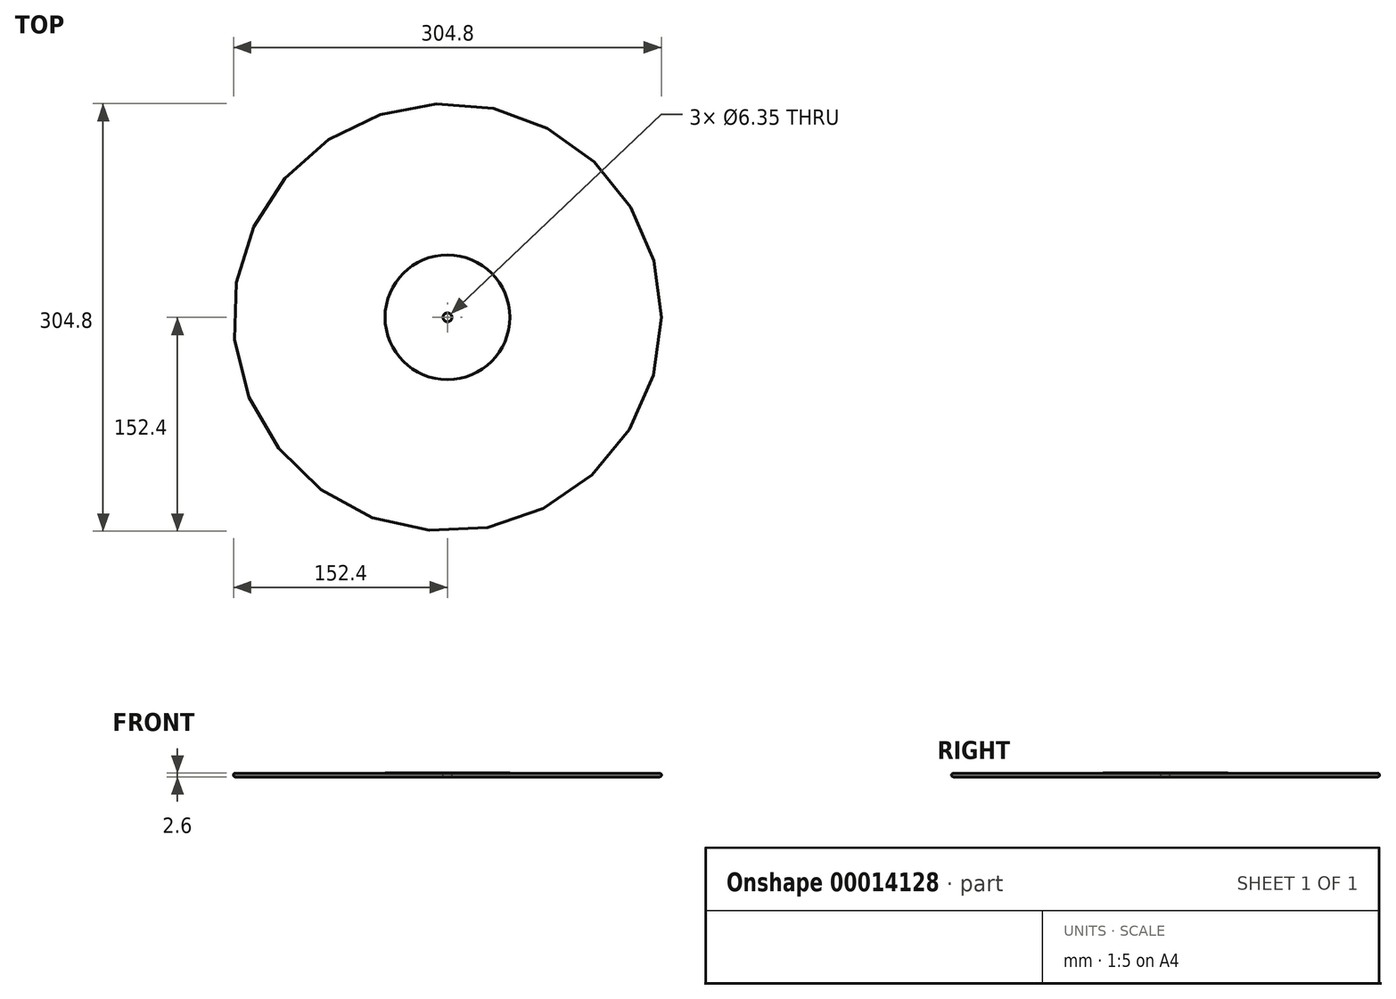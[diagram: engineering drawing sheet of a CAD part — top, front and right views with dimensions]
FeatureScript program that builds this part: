
annotation { "Feature Type Name" : "Feature", "Feature Type Description" : "" }
export const myFeature = defineFeature(function(context is Context, id is Id, definition is map)
    precondition{}
    {
        {
            var Q0;
            Q0=qCreatedBy(makeId("Top.planeOp"),FACE);
            var sketch = newSketch(context, id + "F0", { "sketchPlane" : qUnion([Q0])});
            skCircle(sketch, "E0", {"center": v(0, 0) * mm, "radius": 152.4 * mm});
            skSolve(sketch);
        }
        {
            var Q0;
            Q0 = qSketchRegion(id + "F0", true);
            extrude(context, id + "F1", {"entities" : qUnion([Q0]), "depth" : 2.54 * mm});
        }
        {
            var Q0;
            Q0=makeQuery(id+"F1.opExtrude","CAP_EDGE",EDGE,{"disambiguationData":[OSD([sQuery(id+"F0.wireOp",EDGE,"E0")])],"isStart":false});
            var Q1;
            Q1=makeQuery(id+"F1.opExtrude","CAP_EDGE",EDGE,{"disambiguationData":[OSD([sQuery(id+"F0.wireOp",EDGE,"E0")])],"isStart":true});
            fillet(context, id + "F2", {"entities" : qUnion([Q0, Q1]), "radius" : 1.27 * mm, "tangentPropagation" : true, "allowEdgeOverflow" : false});
        }
        {
            var Q0;
            Q0=makeQuery(id+"F1.opExtrude","CAP_FACE",FACE,{"disambiguationData":[OSD([sQuery(id+"F0.wireOp",EDGE,"E0")])],"isStart":false});
            var sketch = newSketch(context, id + "F3", { "sketchPlane" : qUnion([Q0])});
            skCircle(sketch, "E1", {"center": v(0, 0) * mm, "radius": 44.45 * mm});
            skSolve(sketch);
        }
        {
            var Q0;
            Q0=makeQuery(id+"F3.imprint","IMPRINT",FACE,{"disambiguationData":[TD([[makeQuery(id+"F3.imprint","IMPRINT",EDGE,{"derivedFrom":sQuery(id+"F3.wireOp",EDGE,"E1")}),1.0]])]});
            extrude(context, id + "F4", {"entities" : qUnion([Q0]), "depth" : 0.03 * mm});
        }
        {
            var Q0;
            Q0=makeQuery(id+"F4.opExtrude","CAP_FACE",FACE,{"disambiguationData":[OSD([sQuery(id+"F3.wireOp",EDGE,"E1")])],"isStart":false});
            var sketch = newSketch(context, id + "F5", { "sketchPlane" : qUnion([Q0])});
            skCircle(sketch, "E2", {"center": v(0, 0) * mm, "radius": 3.17 * mm});
            skSolve(sketch);
        }
        {
            var Q0;
            Q0=makeQuery(id+"F5.imprint","IMPRINT",FACE,{"disambiguationData":[TD([[makeQuery(id+"F5.imprint","IMPRINT",EDGE,{"derivedFrom":sQuery(id+"F5.wireOp",EDGE,"E2")}),1.0]])]});
            extrude(context, id + "F6", {"entities" : qUnion([Q0]), "operationType" : NewBodyOperationType.REMOVE, "oppositeDirection" : true, "depth" : 25.4 * mm});
        }
        {
            var Q0;
            Q0=makeQuery(id+"F1.opExtrude","CAP_FACE",FACE,{"disambiguationData":[OSD([sQuery(id+"F0.wireOp",EDGE,"E0")])],"isStart":true});
            var sketch = newSketch(context, id + "F7", { "sketchPlane" : qUnion([Q0])});
            skCircle(sketch, "E3", {"center": v(0, 0) * mm, "radius": 44.45 * mm});
            skSolve(sketch);
        }
        {
            var Q0;
            Q0=makeQuery(id+"F7.imprint","IMPRINT",FACE,{"disambiguationData":[TD([[makeQuery(id+"F7.imprint","IMPRINT",EDGE,{"derivedFrom":sQuery(id+"F7.wireOp",EDGE,"E3")}),1.0]])]});
            extrude(context, id + "F8", {"entities" : qUnion([Q0]), "depth" : 0.03 * mm});
        }
    });
